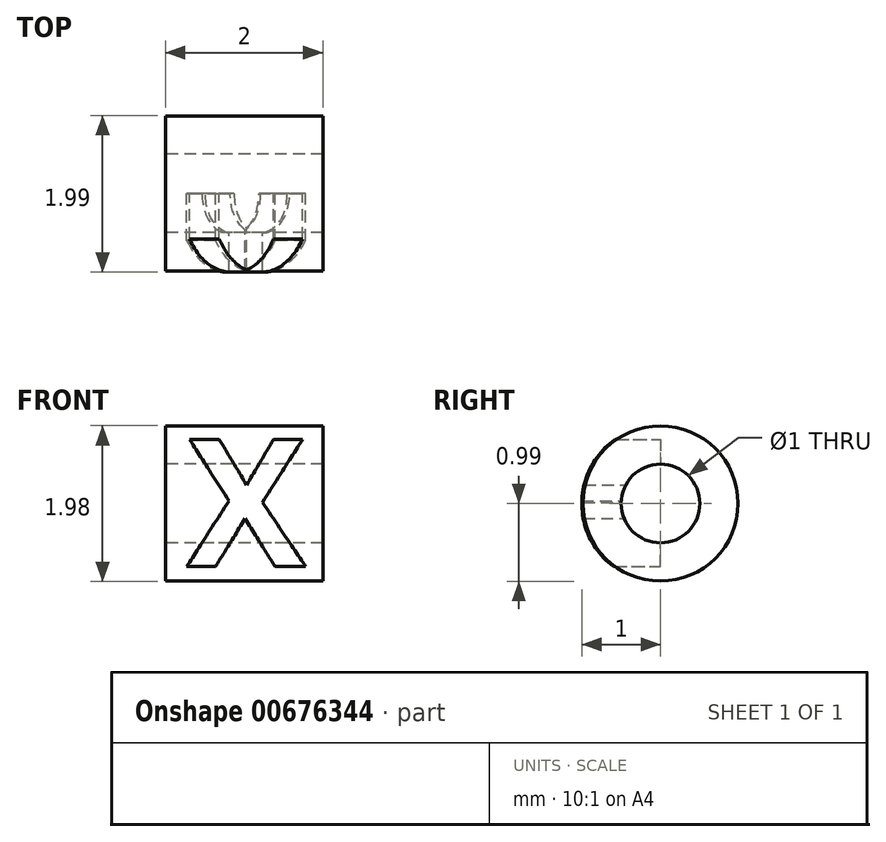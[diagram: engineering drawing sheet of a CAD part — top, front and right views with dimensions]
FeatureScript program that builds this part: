
annotation { "Feature Type Name" : "Feature", "Feature Type Description" : "" }
export const myFeature = defineFeature(function(context is Context, id is Id, definition is map)
    precondition{}
    {
        {
            var Q0;
            Q0=qCreatedBy(makeId("Right.planeOp"),FACE);
            var sketch = newSketch(context, id + "F0", { "sketchPlane" : qUnion([Q0])});
            skCircle(sketch, "E0", {"center": v(0, 0) * mm, "radius": 0.5 * mm});
            skCircle(sketch, "E1", {"center": v(0, 0) * mm, "radius": 1 * mm});
            skCircle(sketch, "E2", {"center": v(0, 0) * mm, "radius": 0.98 * mm});
            skSolve(sketch);
        }
        {
            var Q0;
            Q0=makeQuery(id+"F0.imprint","IMPRINT",FACE,{"disambiguationData":[TD([[makeQuery(id+"F0.imprint","IMPRINT",EDGE,{"derivedFrom":sQuery(id+"F0.wireOp",EDGE,"E0")}),-1.0]])]});
            var Q1;
            Q1=makeQuery(id+"F0.imprint","IMPRINT",FACE,{"disambiguationData":[TD([[makeQuery(id+"F0.imprint","IMPRINT",EDGE,{"derivedFrom":sQuery(id+"F0.wireOp",EDGE,"E1")}),1.0]])]});
            extrude(context, id + "F1", {"entities" : qUnion([Q0, Q1]), "depth" : 2 * mm, "offsetDistance" : 25 * mm});
        }
        {
            var Q0;
            Q0=qCreatedBy(makeId("Front.planeOp"),FACE);
            var sketch = newSketch(context, id + "F2", { "sketchPlane" : qUnion([Q0])});
            skText(sketch, "E3", { "text": "X", "fontName": "OpenSans-Bold.ttf"});
            const initialGuessF2  = {"E3": [0.00027, -0.0008, 1, 0, 0.00163]};
            skSetInitialGuess(sketch, initialGuessF2);
            skSolve(sketch);
        }
        {
            var Q0;
            Q0=qSketchRegion(id+"F2",true);
            var Q1;
            Q1=qConstructionFilter(qBodyType(qCreatedBy(id+"F2",EDGE),BodyType.WIRE),ConstructionObject.NO);
            var Q2;
            Q2=makeQuery(id+"F1.opExtrude","SWEPT_FACE",FACE,{"disambiguationData":[OSD([sQuery(id+"F0.wireOp",EDGE,"E1")])]});
            var Q3;
            Q3=makeQuery(id+"F1.opExtrude","SWEPT_BODY",BODY,{"disambiguationData":[OSD([sQuery(id+"F0.wireOp",EDGE,"E0"),sQuery(id+"F0.wireOp",EDGE,"E1")])]});
            var Q4;
            Q4=sQuery(id+"F0.wireOp",VERTEX,"27635d6e-dcd6-4653-b727-4819003c0945");
            extrude(context, id + "F3", {"entities" : qUnion([Q0]), "operationType" : NewBodyOperationType.INTERSECT, "surfaceEntities" : qUnion([Q1]), "endBound" : BoundingType.UP_TO_SURFACE, "endBoundEntityFace" : qUnion([Q2]), "endBoundEntityBody" : qUnion([Q3]), "endBoundEntityVertex" : qUnion([Q4]), "depth" : 25 * mm, "offsetDistance" : 25 * mm});
        }
        {
            var Q0;
            Q0=makeQuery(id+"F0.imprint","IMPRINT",FACE,{"disambiguationData":[TD([[makeQuery(id+"F0.imprint","IMPRINT",EDGE,{"derivedFrom":sQuery(id+"F0.wireOp",EDGE,"E0")}),-1.0]])]});
            extrude(context, id + "F4", {"entities" : qUnion([Q0]), "depth" : 2 * mm, "offsetDistance" : 25 * mm});
        }
    });
